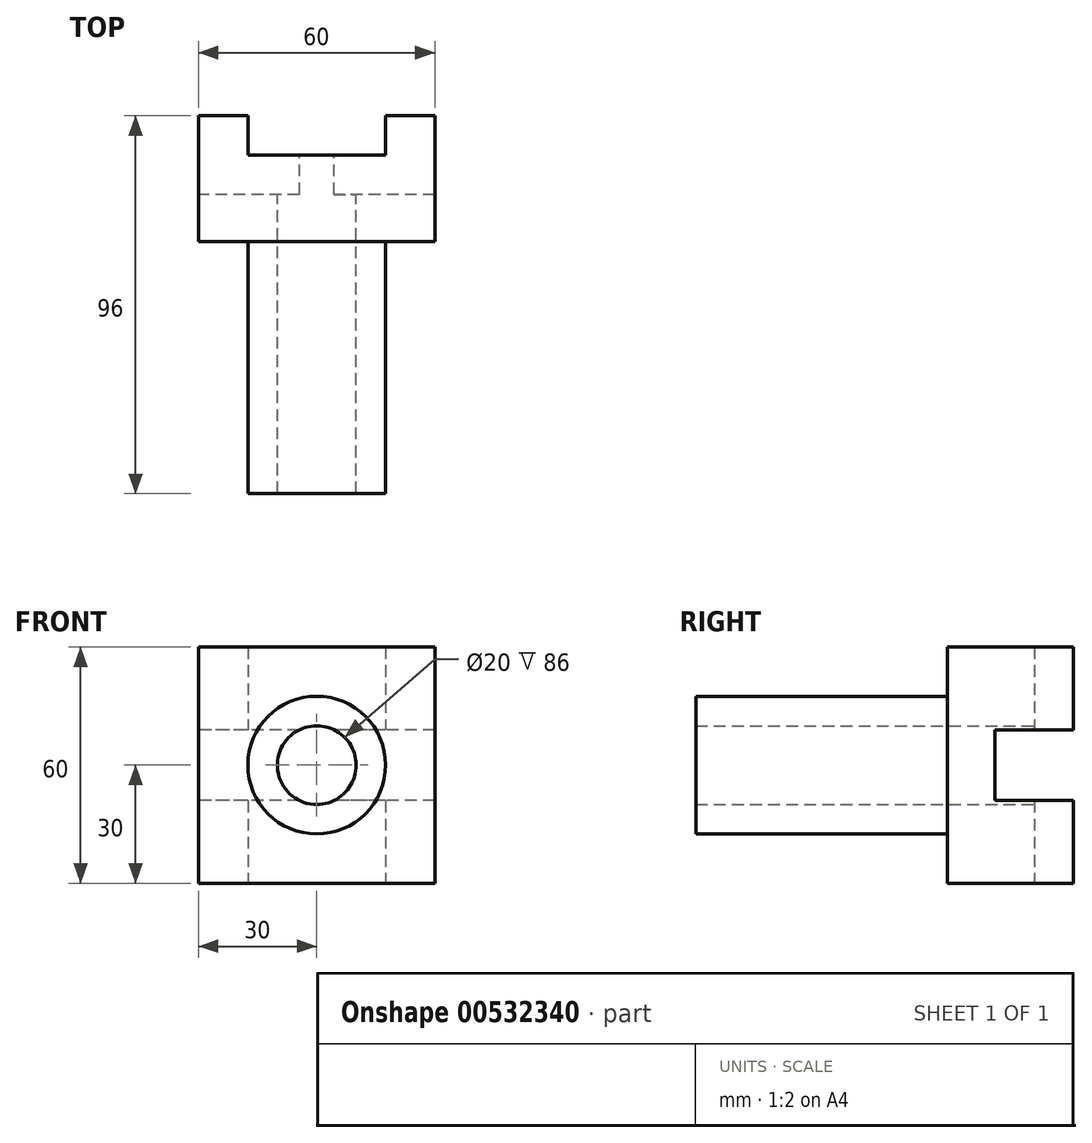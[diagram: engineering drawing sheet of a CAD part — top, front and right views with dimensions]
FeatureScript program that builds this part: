
annotation { "Feature Type Name" : "Feature", "Feature Type Description" : "" }
export const myFeature = defineFeature(function(context is Context, id is Id, definition is map)
    precondition{}
    {
        {
            var Q0;
            Q0=qCreatedBy(makeId("Front.planeOp"),FACE);
            var sketch = newSketch(context, id + "F0", { "sketchPlane" : qUnion([Q0])});
            skCircle(sketch, "E0", {"center": v(0, 0) * mm, "radius": 17.5 * mm});
            skCircle(sketch, "E1", {"center": v(0, 0) * mm, "radius": 10 * mm});
            skSolve(sketch);
        }
        {
            var Q0;
            Q0=makeQuery(id+"F0.imprint","IMPRINT",FACE,{"disambiguationData":[TD([[makeQuery(id+"F0.imprint","IMPRINT",EDGE,{"derivedFrom":sQuery(id+"F0.wireOp",EDGE,"E0")}),1.0]])]});
            extrude(context, id + "F1", {"entities" : qUnion([Q0]), "depth" : (96 - 32) * mm, "offsetDistance" : 25 * mm});
        }
        {
            var Q0;
            Q0=makeQuery(id+"F1.opExtrude","CAP_FACE",FACE,{"disambiguationData":[OSD([sQuery(id+"F0.wireOp",EDGE,"E0"),sQuery(id+"F0.wireOp",EDGE,"E1")])],"isStart":true});
            var sketch = newSketch(context, id + "F2", { "sketchPlane" : qUnion([Q0])});
            skLineSegment(sketch, "E2.bottom", {"start": v(30, 30) * mm, "end": v(-30, 30) * mm});
            skLineSegment(sketch, "E2.top", {"start": v(30, -30) * mm, "end": v(-30, -30) * mm});
            skLineSegment(sketch, "E2.left", {"start": v(30, 30) * mm, "end": v(30, -30) * mm});
            skLineSegment(sketch, "E2.right", {"start": v(-30, 30) * mm, "end": v(-30, -30) * mm});
            skPoint(sketch, "E2.middle", {"position": v(0, 0) * mm});
            skSolve(sketch);
        }
        {
            var Q0;
            Q0=makeQuery(id+"F2.imprint","IMPRINT",FACE,{"disambiguationData":[TD([[makeQuery(id+"F2.imprint","IMPRINT",EDGE,{"derivedFrom":sQuery(id+"F2.wireOp",EDGE,"E2.bottom")}),1.0]])]});
            var Q1;
            Q1=makeQuery(id+"F2.imprint","IMPRINT",FACE,{"disambiguationData":[TD([[makeQuery(id+"F2.imprint","IMPRINT",EDGE,{"derivedFrom":makeQuery(id+"F1.opExtrude","CAP_EDGE",EDGE,{"disambiguationData":[OSD([sQuery(id+"F0.wireOp",EDGE,"E0")])],"isStart":true})}),-1.0]])]});
            extrude(context, id + "F3", {"entities" : qUnion([Q0, Q1]), "operationType" : NewBodyOperationType.ADD, "depth" : 32 * mm, "offsetDistance" : 25 * mm});
        }
        {
            var Q0;
            Q0=makeQuery(id+"F3.opExtrude","SWEPT_FACE",FACE,{"disambiguationData":[OSD([sQuery(id+"F2.wireOp",EDGE,"E2.top")])]});
            var sketch = newSketch(context, id + "F4", { "sketchPlane" : qUnion([Q0])});
            skLineSegment(sketch, "E3", {"start": v(0, 0) * mm, "end": v(0, -32) * mm, "construction": true});
            skLineSegment(sketch, "E4.bottom", {"start": v(-17.5, -32) * mm, "end": v(17.5, -32) * mm});
            skLineSegment(sketch, "E4.top", {"start": v(-17.5, -22) * mm, "end": v(17.5, -22) * mm});
            skLineSegment(sketch, "E4.left", {"start": v(-17.5, -32) * mm, "end": v(-17.5, -22) * mm});
            skLineSegment(sketch, "E4.right", {"start": v(17.5, -32) * mm, "end": v(17.5, -22) * mm});
            skSolve(sketch);
        }
        {
            var Q0;
            Q0=makeQuery(id+"F4.imprint","IMPRINT",FACE,{"disambiguationData":[TD([[makeQuery(id+"F4.imprint","IMPRINT",EDGE,{"derivedFrom":sQuery(id+"F4.wireOp",EDGE,"E4.bottom")}),1.0]])]});
            extrude(context, id + "F5", {"entities" : qUnion([Q0]), "operationType" : NewBodyOperationType.REMOVE, "endBound" : BoundingType.THROUGH_ALL, "oppositeDirection" : true, "depth" : 25 * mm, "offsetDistance" : 25 * mm});
        }
        {
            var Q0;
            Q0=makeQuery(id+"F3.opExtrude","SWEPT_FACE",FACE,{"disambiguationData":[OSD([sQuery(id+"F2.wireOp",EDGE,"E2.left")])]});
            var sketch = newSketch(context, id + "F6", { "sketchPlane" : qUnion([Q0])});
            skLineSegment(sketch, "E5", {"start": v(0, 0) * mm, "end": v(-32, 0) * mm, "construction": true});
            skLineSegment(sketch, "E6.bottom", {"start": v(-32, 9) * mm, "end": v(-12, 9) * mm});
            skLineSegment(sketch, "E6.top", {"start": v(-32, -9) * mm, "end": v(-12, -9) * mm});
            skLineSegment(sketch, "E6.left", {"start": v(-32, 9) * mm, "end": v(-32, -9) * mm});
            skLineSegment(sketch, "E6.right", {"start": v(-12, 9) * mm, "end": v(-12, -9) * mm});
            skSolve(sketch);
        }
        {
            var Q0;
            Q0=makeQuery(id+"F6.imprint","IMPRINT",FACE,{"disambiguationData":[TD([[makeQuery(id+"F6.imprint","IMPRINT",EDGE,{"derivedFrom":sQuery(id+"F6.wireOp",EDGE,"E6.bottom")}),-1.0]])]});
            extrude(context, id + "F7", {"entities" : qUnion([Q0]), "operationType" : NewBodyOperationType.REMOVE, "endBound" : BoundingType.THROUGH_ALL, "oppositeDirection" : true, "depth" : 25 * mm, "offsetDistance" : 25 * mm});
        }
    });
